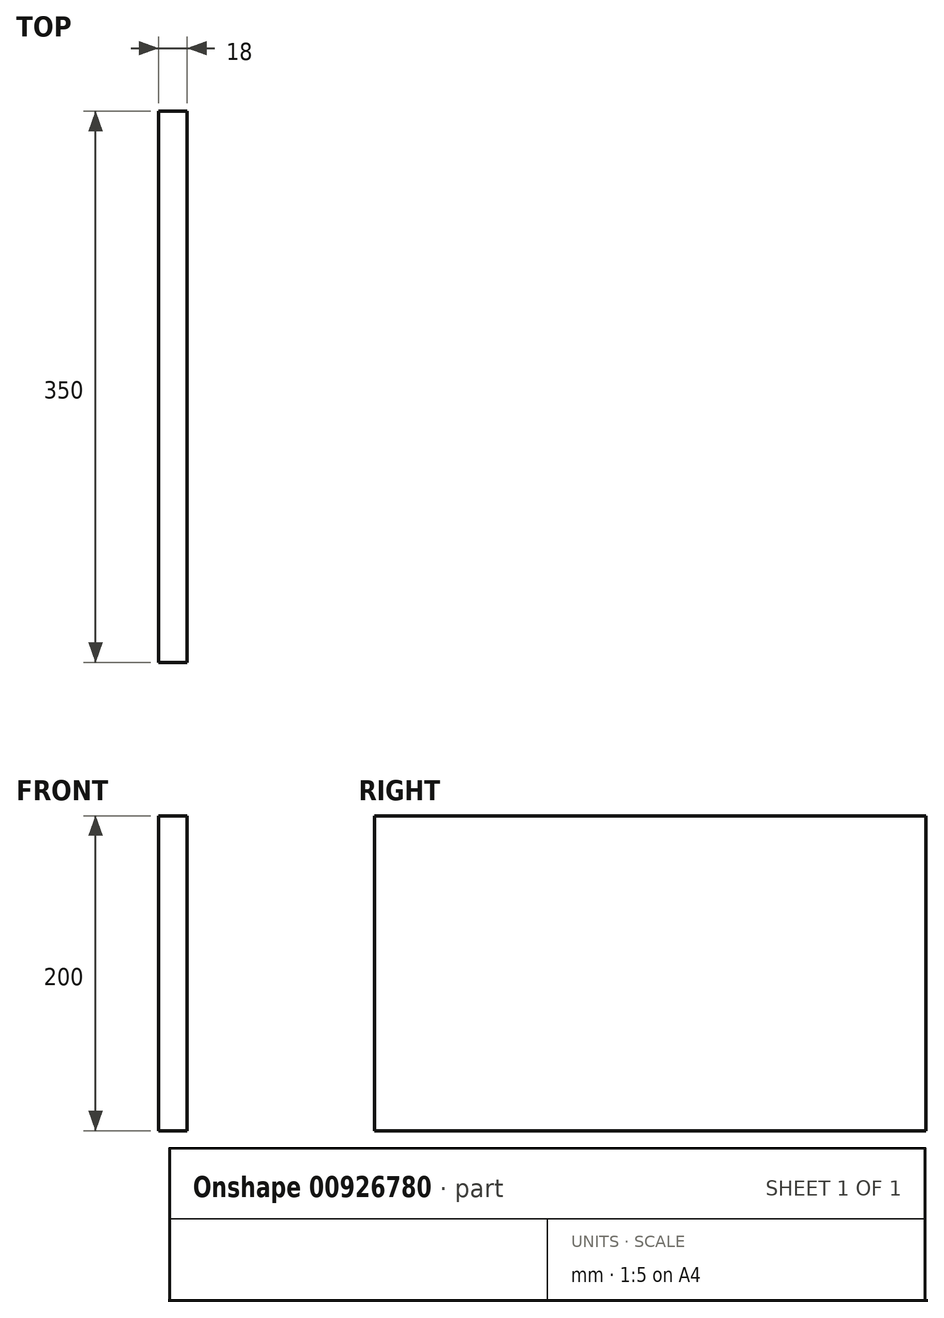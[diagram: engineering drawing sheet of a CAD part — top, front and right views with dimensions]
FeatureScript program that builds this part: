
annotation { "Feature Type Name" : "Feature", "Feature Type Description" : "" }
export const myFeature = defineFeature(function(context is Context, id is Id, definition is map)
    precondition{}
    {
        {
            var Q0;
            Q0=qCreatedBy(makeId("Right.planeOp"),FACE);
            var sketch = newSketch(context, id + "F0", { "sketchPlane" : qUnion([Q0])});
            skLineSegment(sketch, "E0.bottom", {"start": v(175, -100) * mm, "end": v(-175, -100) * mm});
            skLineSegment(sketch, "E0.top", {"start": v(175, 100) * mm, "end": v(-175, 100) * mm});
            skLineSegment(sketch, "E0.left", {"start": v(175, -100) * mm, "end": v(175, 100) * mm});
            skLineSegment(sketch, "E0.right", {"start": v(-175, -100) * mm, "end": v(-175, 100) * mm});
            skPoint(sketch, "E0.middle", {"position": v(0, 0) * mm});
            skSolve(sketch);
        }
        {
            var Q0;
            Q0 = qSketchRegion(id + "F0", true);
            extrude(context, id + "F1", {"entities" : qUnion([Q0]), "endBound" : BoundingType.SYMMETRIC, "depth" : 18 * mm, "offsetDistance" : 25 * mm});
        }
    });
